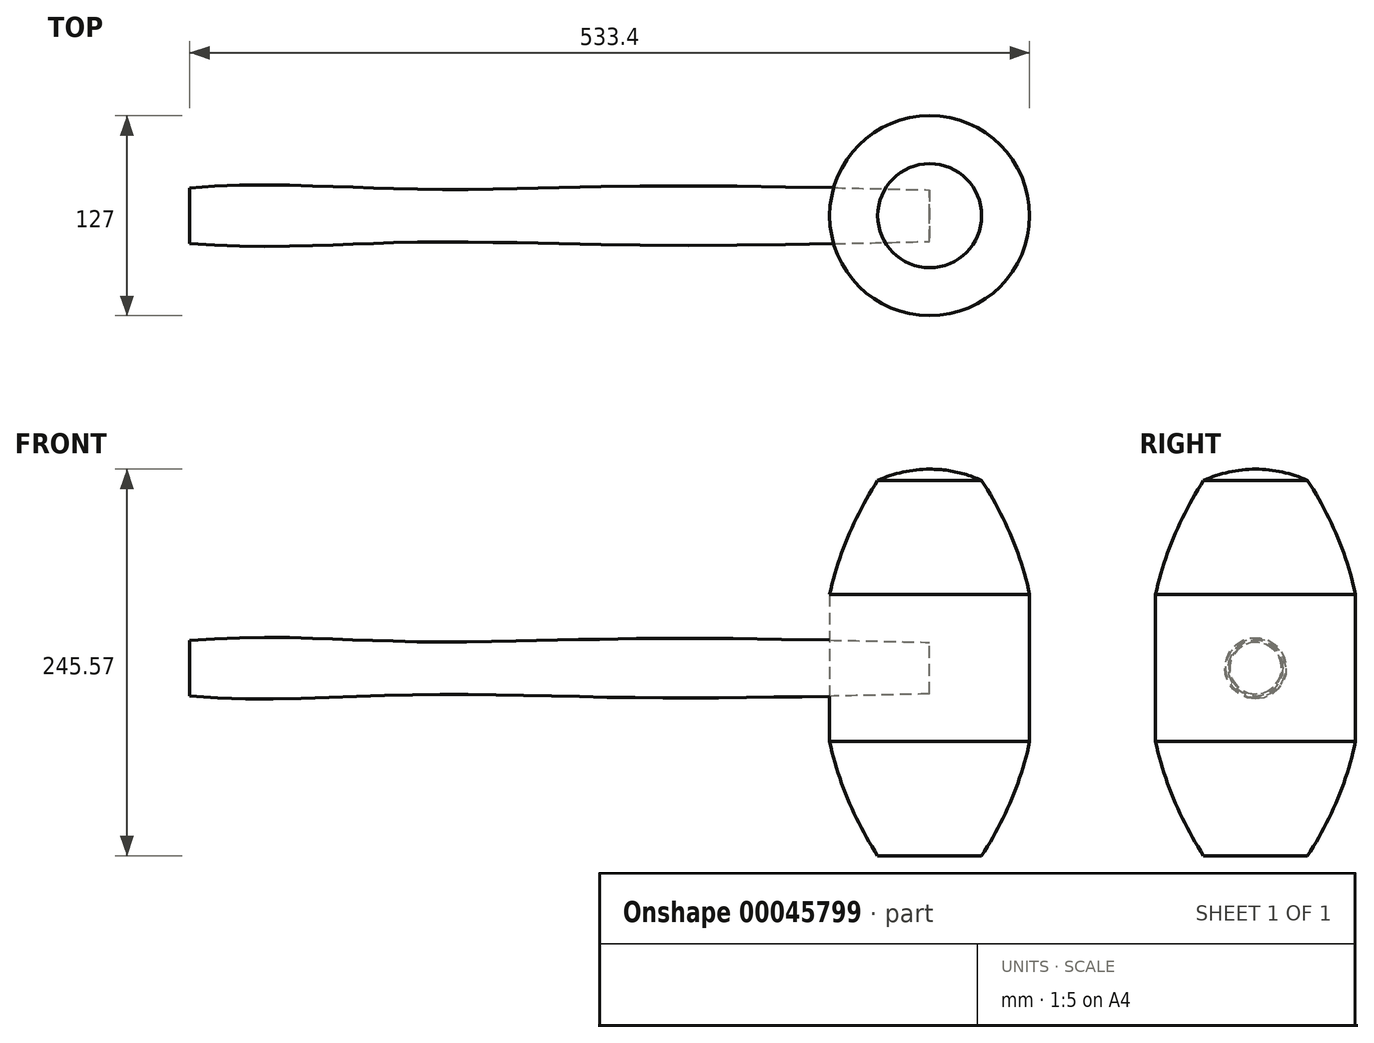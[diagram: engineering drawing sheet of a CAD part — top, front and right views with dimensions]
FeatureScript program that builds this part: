
annotation { "Feature Type Name" : "Feature", "Feature Type Description" : "" }
export const myFeature = defineFeature(function(context is Context, id is Id, definition is map)
    precondition{}
    {
        {
            var Q0;
            Q0=qCreatedBy(makeId("Right.planeOp"),FACE);
            var sketch = newSketch(context, id + "F0", { "sketchPlane" : qUnion([Q0])});
            skCircle(sketch, "E0", {"center": v(0, 0) * mm, "radius": 17.55 * mm});
            skSolve(sketch);
        }
        {
            var Q0;
            Q0=qCreatedBy(makeId("Right.planeOp"),FACE);
            cPlane(context, id + "F1", {"entities" : qUnion([Q0]), "cplaneType" : CPlaneType.OFFSET, "offset" : 12.7 * mm, "width" : 152.4 * mm, "height" : 152.4 * mm});
        }
        {
            var Q0;
            Q0=qCreatedBy(id+"F1.planeOp",FACE);
            var sketch = newSketch(context, id + "F2", { "sketchPlane" : qUnion([Q0])});
            skCircle(sketch, "E1", {"center": v(0, 0) * mm, "radius": 18.5 * mm});
            skSolve(sketch);
        }
        {
            var Q0;
            Q0=qCreatedBy(id+"F1.planeOp",FACE);
            cPlane(context, id + "F3", {"entities" : qUnion([Q0]), "cplaneType" : CPlaneType.OFFSET, "offset" : 127 * mm, "width" : 152.4 * mm, "height" : 152.4 * mm});
        }
        {
            var Q0;
            Q0=qCreatedBy(id+"F3.planeOp",FACE);
            var sketch = newSketch(context, id + "F4", { "sketchPlane" : qUnion([Q0])});
            skCircle(sketch, "E2", {"center": v(0, 0) * mm, "radius": 16.88 * mm});
            skSolve(sketch);
        }
        {
            var Q0;
            Q0=qCreatedBy(id+"F3.planeOp",FACE);
            cPlane(context, id + "F5", {"entities" : qUnion([Q0]), "cplaneType" : CPlaneType.OFFSET, "offset" : 127 * mm, "width" : 152.4 * mm, "height" : 152.4 * mm});
        }
        {
            var Q0;
            Q0=qCreatedBy(id+"F5.planeOp",FACE);
            var sketch = newSketch(context, id + "F6", { "sketchPlane" : qUnion([Q0])});
            skCircle(sketch, "E3.0", {"center": v(0, 0) * mm, "radius": 18.5 * mm});
            skSolve(sketch);
        }
        {
            var Q0;
            Q0=qCreatedBy(id+"F5.planeOp",FACE);
            cPlane(context, id + "F7", {"entities" : qUnion([Q0]), "cplaneType" : CPlaneType.OFFSET, "offset" : 203.2 * mm, "width" : 152.4 * mm, "height" : 152.4 * mm});
        }
        {
            var Q0;
            Q0=qCreatedBy(id+"F7.planeOp",FACE);
            var sketch = newSketch(context, id + "F8", { "sketchPlane" : qUnion([Q0])});
            skCircle(sketch, "E4", {"center": v(0, 0) * mm, "radius": 16.38 * mm});
            skSolve(sketch);
        }
        {
            var Q0;
            Q0=makeQuery(id+"F8.imprint","IMPRINT",FACE,{"disambiguationData":[TD([[makeQuery(id+"F8.imprint","IMPRINT",EDGE,{"derivedFrom":sQuery(id+"F8.wireOp",EDGE,"E4")}),1.0]])]});
            var Q1;
            Q1=makeQuery(id+"F6.imprint","IMPRINT",FACE,{"disambiguationData":[TD([[makeQuery(id+"F6.imprint","IMPRINT",EDGE,{"derivedFrom":sQuery(id+"F6.wireOp",EDGE,"E3.0")}),1.0]])]});
            var Q2;
            Q2=makeQuery(id+"F4.imprint","IMPRINT",FACE,{"disambiguationData":[TD([[makeQuery(id+"F4.imprint","IMPRINT",EDGE,{"derivedFrom":sQuery(id+"F4.wireOp",EDGE,"E2")}),1.0]])]});
            var Q3;
            Q3=makeQuery(id+"F2.imprint","IMPRINT",FACE,{"disambiguationData":[TD([[makeQuery(id+"F2.imprint","IMPRINT",EDGE,{"derivedFrom":sQuery(id+"F2.wireOp",EDGE,"E1")}),1.0]])]});
            var Q4;
            Q4=makeQuery(id+"F0.imprint","IMPRINT",FACE,{"disambiguationData":[TD([[makeQuery(id+"F0.imprint","IMPRINT",EDGE,{"derivedFrom":sQuery(id+"F0.wireOp",EDGE,"E0")}),1.0]])]});
            loft(context, id + "F9", {"sheetProfilesArray" : [{ "sheetProfileEntities" : qUnion([Q0]) }, { "sheetProfileEntities" : qUnion([Q1]) }, { "sheetProfileEntities" : qUnion([Q2]) }, { "sheetProfileEntities" : qUnion([Q3]) }, { "sheetProfileEntities" : qUnion([Q4]) }]});
        }
        {
            var Q0;
            Q0=makeQuery(id+"F9.opLoft","CAP_FACE",FACE,{"disambiguationData":[OSD([makeQuery(id+"F8.imprint","IMPRINT",FACE,{"disambiguationData":[TD([[makeQuery(id+"F8.imprint","IMPRINT",EDGE,{"derivedFrom":sQuery(id+"F8.wireOp",EDGE,"E4")}),1.0]])]})])],"isStart":true});
            var sketch = newSketch(context, id + "F10", { "sketchPlane" : qUnion([Q0])});
            skFitSpline(sketch, "E5.0", {"points": [v(16.38, 0) * mm, v(16.38, -1.02) * mm, v(16.28, -2.09) * mm, v(16.08, -3.14) * mm, v(16.07, -3.2) * mm, v(15.87, -4.2) * mm, v(15.56, -5.22) * mm, v(15.16, -6.22) * mm, v(15.13, -6.27) * mm, v(14.74, -7.21) * mm, v(14.25, -8.16) * mm, v(13.65, -9.05) * mm, v(13.62, -9.1) * mm, v(13.06, -9.95) * mm, v(12.38, -10.78) * mm, v(11.62, -11.54) * mm, v(11.58, -11.58) * mm, v(10.86, -12.3) * mm, v(10.04, -12.99) * mm, v(9.15, -13.59) * mm, v(9.1, -13.62) * mm, v(8.25, -14.19) * mm, v(7.31, -14.7) * mm, v(6.32, -15.11) * mm, v(6.27, -15.13) * mm, v(5.33, -15.52) * mm, v(4.3, -15.84) * mm, v(3.25, -16.06) * mm, v(3.2, -16.07) * mm, v(2.2, -16.27) * mm, v(1.13, -16.38) * mm, v(0.06, -16.38) * mm, v(0, -16.38) * mm, v(-1.02, -16.38) * mm, v(-2.08, -16.28) * mm, v(-3.14, -16.08) * mm, v(-3.2, -16.07) * mm, v(-4.2, -15.87) * mm, v(-5.22, -15.56) * mm, v(-6.22, -15.16) * mm, v(-6.27, -15.13) * mm, v(-7.21, -14.74) * mm, v(-8.16, -14.25) * mm, v(-9.05, -13.65) * mm, v(-9.1, -13.62) * mm, v(-9.95, -13.06) * mm, v(-10.78, -12.38) * mm, v(-11.54, -11.62) * mm, v(-11.58, -11.58) * mm, v(-12.3, -10.86) * mm, v(-12.99, -10.04) * mm, v(-13.59, -9.15) * mm, v(-13.62, -9.1) * mm, v(-14.19, -8.25) * mm, v(-14.7, -7.31) * mm, v(-15.11, -6.32) * mm, v(-15.13, -6.27) * mm, v(-15.52, -5.33) * mm, v(-15.84, -4.3) * mm, v(-16.06, -3.25) * mm, v(-16.07, -3.2) * mm, v(-16.27, -2.2) * mm, v(-16.38, -1.13) * mm, v(-16.38, -0.06) * mm, v(-16.38, 0) * mm, v(-16.38, 1.02) * mm, v(-16.28, 2.08) * mm, v(-16.08, 3.14) * mm, v(-16.07, 3.2) * mm, v(-15.87, 4.2) * mm, v(-15.56, 5.22) * mm, v(-15.16, 6.22) * mm, v(-15.13, 6.27) * mm, v(-14.74, 7.21) * mm, v(-14.25, 8.16) * mm, v(-13.65, 9.05) * mm, v(-13.62, 9.1) * mm, v(-13.06, 9.95) * mm, v(-12.38, 10.78) * mm, v(-11.62, 11.54) * mm, v(-11.58, 11.58) * mm, v(-10.86, 12.3) * mm, v(-10.04, 12.99) * mm, v(-9.15, 13.59) * mm, v(-9.1, 13.62) * mm, v(-8.25, 14.19) * mm, v(-7.31, 14.7) * mm, v(-6.32, 15.11) * mm, v(-6.27, 15.13) * mm, v(-5.33, 15.52) * mm, v(-4.3, 15.84) * mm, v(-3.25, 16.06) * mm, v(-3.2, 16.07) * mm, v(-2.2, 16.27) * mm, v(-1.13, 16.38) * mm, v(-0.06, 16.38) * mm, v(0, 16.38) * mm, v(1.02, 16.38) * mm, v(2.08, 16.28) * mm, v(3.14, 16.08) * mm, v(3.2, 16.07) * mm, v(4.2, 15.87) * mm, v(5.22, 15.56) * mm, v(6.22, 15.16) * mm, v(6.27, 15.13) * mm, v(7.21, 14.74) * mm, v(8.16, 14.25) * mm, v(9.05, 13.65) * mm, v(9.1, 13.62) * mm, v(9.95, 13.06) * mm, v(10.78, 12.38) * mm, v(11.54, 11.62) * mm, v(11.58, 11.58) * mm, v(12.3, 10.86) * mm, v(12.99, 10.04) * mm, v(13.59, 9.15) * mm, v(13.62, 9.1) * mm, v(14.19, 8.25) * mm, v(14.7, 7.31) * mm, v(15.11, 6.32) * mm, v(15.13, 6.27) * mm, v(15.52, 5.33) * mm, v(15.84, 4.3) * mm, v(16.06, 3.25) * mm, v(16.07, 3.2) * mm, v(16.28, 2.14) * mm, v(16.38, 1.08) * mm, v(16.38, 0) * mm, v(16.38, 0) * mm]});
            skSolve(sketch);
        }
        {
            var Q0;
            Q0=qCreatedBy(makeId("Front.planeOp"),FACE);
            var sketch = newSketch(context, id + "F11", { "sketchPlane" : qUnion([Q0])});
            skLineSegment(sketch, "E6.0", {"start": v(469.9, 16.38) * mm, "end": v(469.9, -16.38) * mm});
            skLineSegment(sketch, "E7", {"start": v(469.9, 16.38) * mm, "end": v(469.9, 119.18) * mm});
            skLineSegment(sketch, "E8", {"start": v(0, 0) * mm, "end": v(-39.35, 0) * mm});
            skLineSegment(sketch, "E9.MirrorCS", {"start": v(469.9, -16.38) * mm, "end": v(469.9, -119.18) * mm});
            skPoint(sketch, "E10", {"position": v(533.4, 16.38) * mm});
            skPoint(sketch, "E11", {"position": v(580.97, -16.38) * mm});
            skPoint(sketch, "E12", {"position": v(533.4, 46.67) * mm});
            skPoint(sketch, "E13.MirrorP", {"position": v(533.4, -46.67) * mm});
            skLineSegment(sketch, "E14", {"start": v(469.9, 119.18) * mm, "end": v(502.92, 119.18) * mm});
            skLineSegment(sketch, "E15.MirrorCS", {"start": v(469.9, -119.18) * mm, "end": v(502.92, -119.18) * mm});
            skLineSegment(sketch, "E16", {"start": v(533.4, 46.67) * mm, "end": v(533.4, -46.67) * mm});
            skArc(sketch, "E17", {"start": v(533.4, 46.67) * mm, "mid": v(521.46, 84.31) * mm, "end": v(502.92, 119.18) * mm});
            skArc(sketch, "E18.MirrorCS", {"start": v(533.4, -46.67) * mm, "mid": v(521.46, -84.31) * mm, "end": v(502.92, -119.18) * mm});
            skLineSegment(sketch, "E19.MirrorCS", {"start": v(469.9, 119.18) * mm, "end": v(436.88, 119.18) * mm});
            skArc(sketch, "E20.MirrorCS", {"start": v(406.4, 46.67) * mm, "mid": v(418.34, 84.31) * mm, "end": v(436.88, 119.18) * mm});
            skLineSegment(sketch, "E21.MirrorCS", {"start": v(406.4, 46.67) * mm, "end": v(406.4, -46.67) * mm});
            skArc(sketch, "E22.MirrorCS", {"start": v(406.4, -46.67) * mm, "mid": v(418.34, -84.31) * mm, "end": v(436.88, -119.18) * mm});
            skLineSegment(sketch, "E23.MirrorCS", {"start": v(469.9, -119.18) * mm, "end": v(436.88, -119.18) * mm});
            skArc(sketch, "E24", {"start": v(502.92, 119.18) * mm, "mid": v(469.9, 126.39) * mm, "end": v(436.88, 119.18) * mm});
            skArc(sketch, "E25.MirrorCS", {"start": v(502.92, -119.18) * mm, "mid": v(469.9, -126.39) * mm, "end": v(436.88, -119.18) * mm});
            skLineSegment(sketch, "E26", {"start": v(469.9, -165.5) * mm, "end": v(469.9, 180.98) * mm});
            skSolve(sketch);
        }
        {
            var Q0;
            {var subQ3=sQuery(id+"F11.wireOp",EDGE,"E14");Q0=makeQuery(id+"F11.imprint","IMPRINT",FACE,{"disambiguationData":[TD([[makeQuery(id+"F11.imprint","IMPRINT",EDGE,{"derivedFrom":subQ3}),1.0]])]});}
            var Q1;
            {var subQ3=sQuery(id+"F11.wireOp",EDGE,"E15.MirrorCS");Q1=makeQuery(id+"F11.imprint","IMPRINT",FACE,{"disambiguationData":[TD([[makeQuery(id+"F11.imprint","IMPRINT",EDGE,{"derivedFrom":subQ3}),-1.0]])]});}
            var Q2;
            {var subQ4=sQuery(id+"F11.wireOp",EDGE,"E14");Q2=makeQuery(id+"F11.imprint","IMPRINT",FACE,{"disambiguationData":[TD([[makeQuery(id+"F11.imprint","IMPRINT",EDGE,{"derivedFrom":subQ4}),-1.0]])]});}
            var Q3;
            Q3=sQuery(id+"F11.wireOp",EDGE,"E26");
            revolve(context, id + "F12", {"entities" : qUnion([Q0, Q1, Q2]), "axis" : qUnion([Q3]), "revolveType" : RevolveType.FULL});
        }
    });
